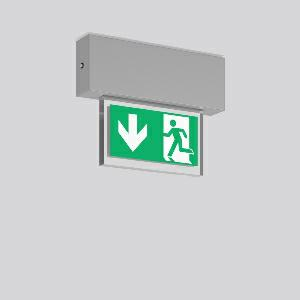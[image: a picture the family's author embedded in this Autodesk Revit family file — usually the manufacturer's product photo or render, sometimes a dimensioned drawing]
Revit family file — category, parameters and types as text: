
# Revit family: halyxx_671504_002_1_8560
name_source: partatom
category: Lighting Fixtures
units: mm (PartAtom-declared; Revit-internal decimal feet)

## family parameters
Cut with Voids When Loaded = No
Host = Face
Light Source = No
Part Type = Normal
Room Calculation Point = No
Round Connector Dimension = Use Diameter
Shared = No

## types (1)
- HALYXX (1 x LED Modul 840, 45 lm, 4000)
    Apparent Load = 2 VA
    Approval mark = CE
    CIE Flux Codes = 18 46 75 53 100
    Color Rendering = 80
    Color Temperature = 4000
    Default Elevation = 1800 mm
    Description = Series: HALYXX
Luminaire for escape route identification. Housing: extruded aluminium profile, anodised or powder-coated. Display panel: highly transparent panel, plastic, with legend on one side/both sides. Driver integrated. Suitable for connection to central battery systems. Please indicate legend number when placing your order! 
Colour: white
Length: 233 mm
Width: 40 mm
Height: 184 mm
Weight: 0.89 kg
Operating mode: maintained power mode
Viewing Distance: 14 m
Lamp: LED
Socket: without socket
Colour temperature: 4000K
Colour rendering index (CRI): 80
System power: 2 W
Rated luminous flux: 45 lm
Luminous flux, emergency: 45
System power, emergency: 1.8 W
Control gear: Regulated power supply
Protection class: I
Type of protection: IP 40
    Height = 184 mm
    Lamp = 1 x LED Modul 840
    Lamp Light Flux = 45 lm
    Lamp count = 1
    Length = 233 mm
    Lifetime = 50000 h
    Luminous efficacy = 23 lm/W
    Manufacturer = RZB
    ModVariant = No
    Model = 671504.002.1
    Mounting Place = Ceiling
    Mounting Type = Surface mounted
    Number of Poles = 1
    OnlyDefault = Yes
    Power Factor = 1
    Product Name = HALYXX
    Product group = Surface mounted ceiling luminaires
    ProductGroupID = 303
    Protection Class = Protection class I
    Protection Degree = IP 40
    RLX_Detail_Level = 1
    RLX_Emergency_Light_Flux = 45 lm
    RLX_Emergency_Type = 3
    RLX_Emergency_Type_DB = Yes
    RlxData = <blob elided: 36477 chars, md5=d3ebfe80>
    Socket = socket
    Standby Power = 0 W
    System Light Flux = 45 lm
    System Power = 2 W
    Type Comments = Product without accessories
    Type Image = 671502.004.jpg
    URL = http://relux.com
    VarID = ---
    Voltage = 230 V
    Voltage Range = 220-240 V
    Weight = 0.00 kg
    Width = 40 mm  [stored 0.131234 ft]

note: [stored X ft] marks values corroborated as IEEE doubles in the binary element streams (Revit-internal decimal feet)

## geometry (parser evidence)
native form markers: Blend x4, Sweep x15
no freeform markers — native parametric forms only
